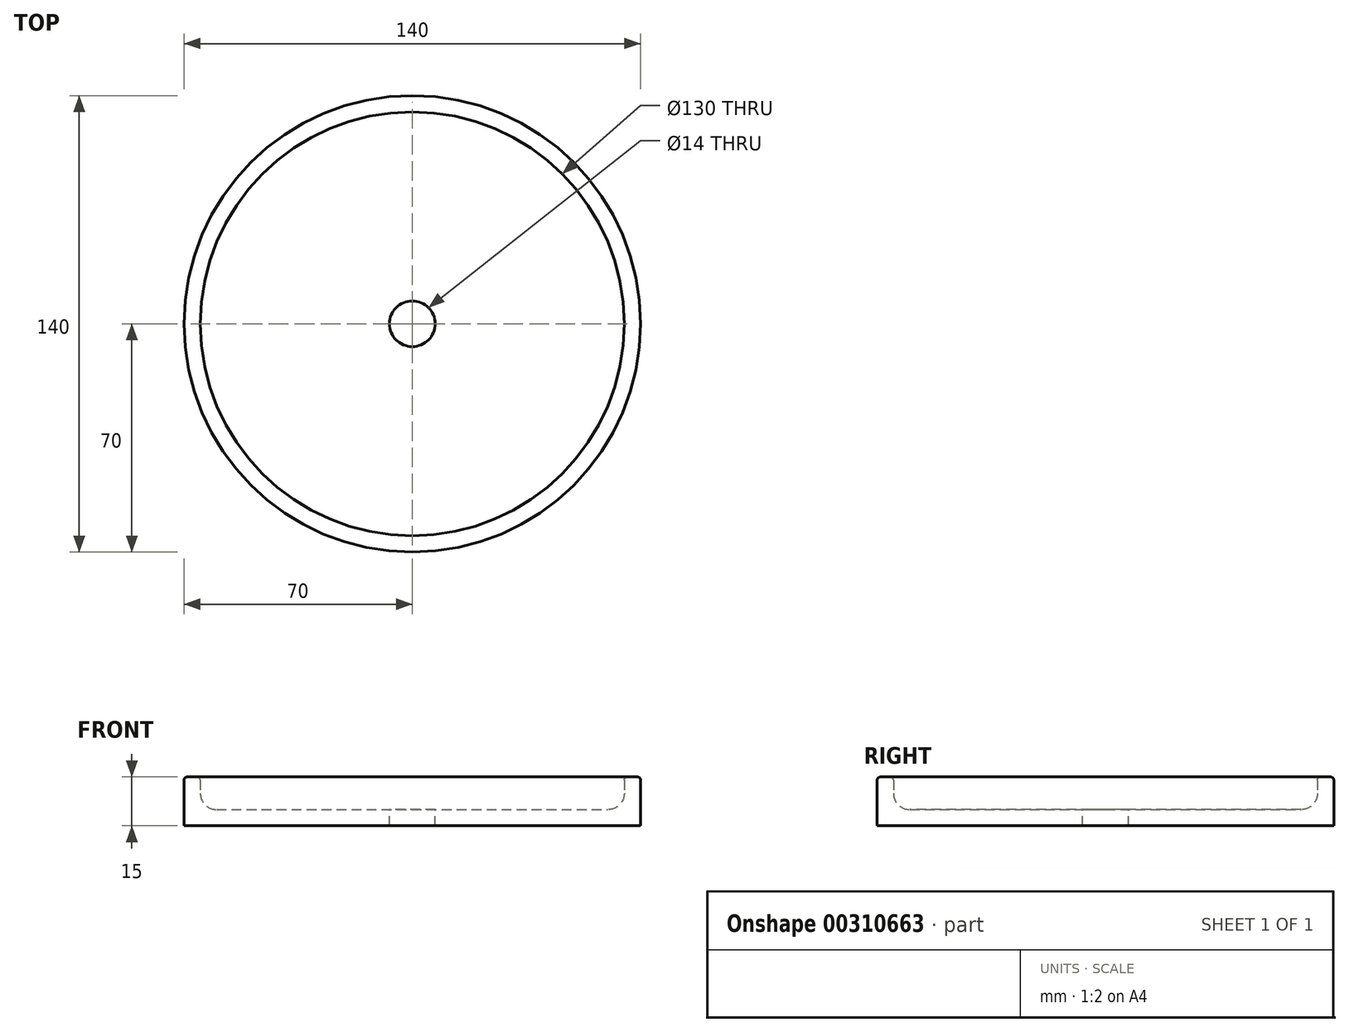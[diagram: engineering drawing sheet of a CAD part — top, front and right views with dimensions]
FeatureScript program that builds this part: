
annotation { "Feature Type Name" : "Feature", "Feature Type Description" : "" }
export const myFeature = defineFeature(function(context is Context, id is Id, definition is map)
    precondition{}
    {
        {
            var Q0;
            Q0=qCreatedBy(makeId("Front.planeOp"),FACE);
            var sketch = newSketch(context, id + "F0", { "sketchPlane" : qUnion([Q0])});
            skLineSegment(sketch, "E0", {"start": v(0, 0) * mm, "end": v(0, 5) * mm});
            skLineSegment(sketch, "E1", {"start": v(0, 5) * mm, "end": v(60, 5) * mm});
            skLineSegment(sketch, "E2", {"start": v(65, 10) * mm, "end": v(65, 14) * mm});
            skLineSegment(sketch, "E3", {"start": v(66, 15) * mm, "end": v(69, 15) * mm});
            skLineSegment(sketch, "E4", {"start": v(70, 14) * mm, "end": v(70, 0) * mm});
            skLineSegment(sketch, "E5", {"start": v(70, 0) * mm, "end": v(0, 0) * mm});
            skPoint(sketch, "E6.visualSharp", {"position": v(65, 5) * mm});
            skArc(sketch, "E6.filletArc", {"start": v(60, 5) * mm, "mid": v(63.54, 6.46) * mm, "end": v(65, 10) * mm});
            skPoint(sketch, "E7.visualSharp", {"position": v(65, 15) * mm});
            skArc(sketch, "E7.filletArc", {"start": v(66, 15) * mm, "mid": v(65.3, 14.7) * mm, "end": v(65, 14) * mm});
            skPoint(sketch, "E8.visualSharp", {"position": v(70, 15) * mm});
            skArc(sketch, "E8.filletArc", {"start": v(70, 14) * mm, "mid": v(69.7, 14.7) * mm, "end": v(69, 15) * mm});
            skLineSegment(sketch, "E9", {"start": v(0, -32.82) * mm, "end": v(0, 53.22) * mm, "construction": true});
            skSolve(sketch);
        }
        {
            var Q0;
            Q0 = qSketchRegion(id + "F0", true);
            var Q1;
            Q1=sQuery(id+"F0.wireOp",EDGE,"E9");
            revolve(context, id + "F1", {"entities" : qUnion([Q0]), "axis" : qUnion([Q1]), "revolveType" : RevolveType.FULL});
        }
        {
            var Q0;
            Q0=makeQuery(id+"F1.opRevolve","SWEPT_FACE",FACE,{"disambiguationData":[OSD([sQuery(id+"F0.wireOp",EDGE,"E1")])]});
            var sketch = newSketch(context, id + "F2", { "sketchPlane" : qUnion([Q0])});
            skCircle(sketch, "E10", {"center": v(0, 0) * mm, "radius": 7 * mm});
            skSolve(sketch);
        }
        {
            var Q0;
            Q0 = qSketchRegion(id + "F2", true);
            extrude(context, id + "F3", {"entities" : qUnion([Q0]), "operationType" : NewBodyOperationType.REMOVE, "oppositeDirection" : true, "depth" : 25 * mm});
        }
    });
